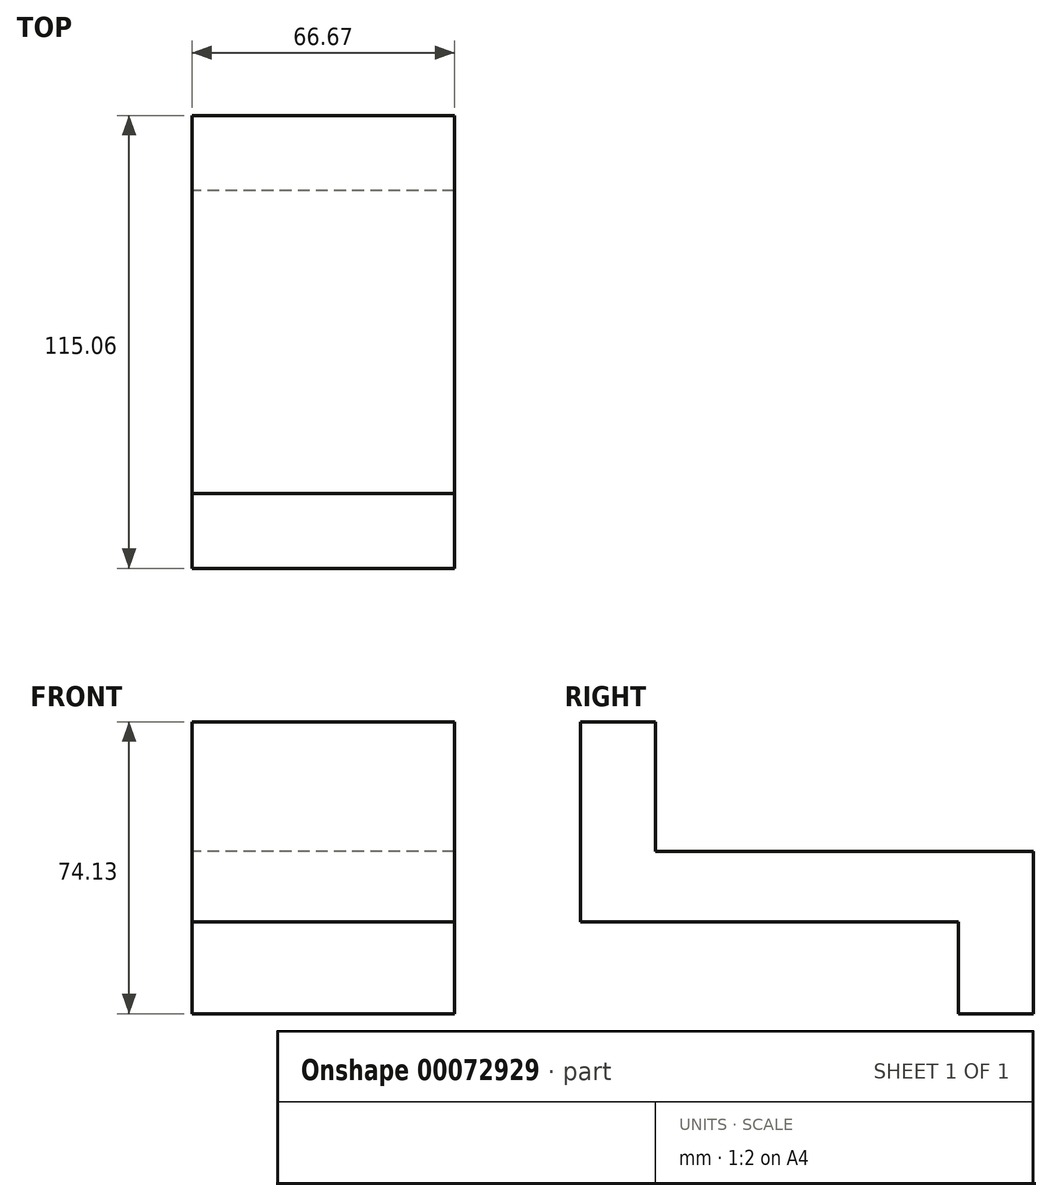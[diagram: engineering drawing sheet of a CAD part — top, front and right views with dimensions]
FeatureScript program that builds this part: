
annotation { "Feature Type Name" : "Feature", "Feature Type Description" : "" }
export const myFeature = defineFeature(function(context is Context, id is Id, definition is map)
    precondition{}
    {
        {
            var Q0;
            Q0=qCreatedBy(makeId("Right.planeOp"),FACE);
            var sketch = newSketch(context, id + "F0", { "sketchPlane" : qUnion([Q0])});
            skLineSegment(sketch, "E0", {"start": v(-71.9, 57.18) * mm, "end": v(-71.9, 6.38) * mm});
            skLineSegment(sketch, "E1", {"start": v(-71.9, 6.38) * mm, "end": v(24.12, 6.38) * mm});
            skLineSegment(sketch, "E2", {"start": v(24.12, 6.38) * mm, "end": v(24.12, -16.95) * mm});
            skLineSegment(sketch, "E3", {"start": v(24.12, -16.95) * mm, "end": v(43.17, -16.95) * mm});
            skLineSegment(sketch, "E4", {"start": v(43.17, -16.95) * mm, "end": v(43.17, 24.33) * mm});
            skLineSegment(sketch, "E5", {"start": v(43.17, 24.33) * mm, "end": v(-52.84, 24.33) * mm});
            skLineSegment(sketch, "E6", {"start": v(-52.84, 24.33) * mm, "end": v(-52.84, 57.18) * mm});
            skLineSegment(sketch, "E7", {"start": v(-52.84, 57.18) * mm, "end": v(-71.9, 57.18) * mm});
            skSolve(sketch);
        }
        {
            var Q0;
            Q0=makeQuery(id+"F0.imprint","IMPRINT",FACE,{"disambiguationData":[TD([[makeQuery(id+"F0.imprint","IMPRINT",EDGE,{"derivedFrom":sQuery(id+"F0.wireOp",EDGE,"E0")}),1.0]])]});
            extrude(context, id + "F1", {"entities" : qUnion([Q0]), "depth" : 66.67 * mm});
        }
    });
